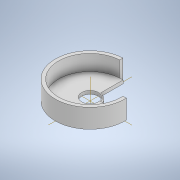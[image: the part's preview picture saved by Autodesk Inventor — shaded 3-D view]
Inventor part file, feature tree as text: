
AUTODESK INVENTOR PART (.ipt)
format: ipt  version: 2022 (Build 260153000, 153)  size: 165,888 bytes
history: native  units: in
note: dims shown in document units (in); Inventor stores cm internally (conversion verified against a paired STEP export)
features: extrude x2, chamfer x1, sketch x1
ambient origin geometry x8: Origin, YZ Plane, XZ Plane, XY Plane, X Axis, Y Axis, Z Axis, Center Point
bodies: Body1 (feature_tree)
feature tree (4):
  extrude  "Extrusion5"  Depth=0.0787in
  chamfer  "Chamfer1"  Distance=0.0394in
  extrude  "Extrusion8"  Depth=0.0787in
  sketch  "Sketch9"  dims[d30=1.6535in d31=0.0394in d32=0.0394in d33=0.0394in d34=0.0394in d35=0.3937in d36=0.0787in d37=0.0in d38=0.4724in d39=0.0197in d40=0.0394in d41=45.0deg d42=0.0787in d50=0.0787in d53=1.4961in d58=1.6535in d60=0.748in d61=0.4528in d62=0.0in d63=0.0394in d64=0.0787in d23=0.5in d24=0.0344in d25=0.5in d26=0.0344in d43=0.0in d44=0.0in d45=0.0in]
